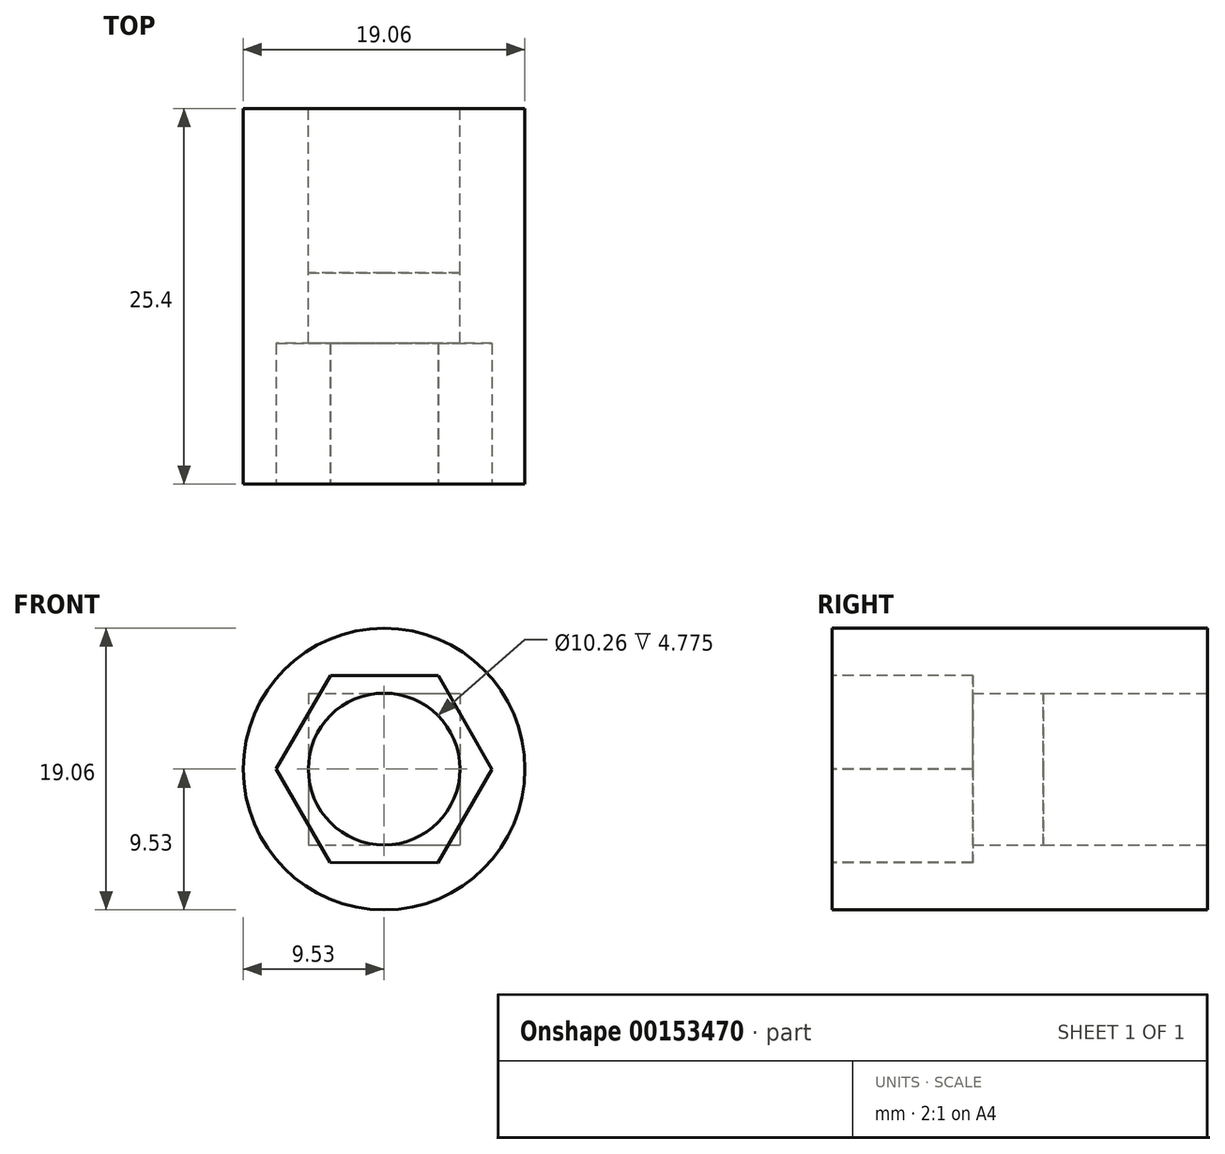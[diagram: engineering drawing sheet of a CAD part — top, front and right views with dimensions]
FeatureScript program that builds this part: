
annotation { "Feature Type Name" : "Feature", "Feature Type Description" : "" }
export const myFeature = defineFeature(function(context is Context, id is Id, definition is map)
    precondition{}
    {
        {
            var Q0;
            Q0=qCreatedBy(makeId("Front.planeOp"),FACE);
            var sketch = newSketch(context, id + "F0", { "sketchPlane" : qUnion([Q0])});
            skCircle(sketch, "E0", {"center": v(0, 0) * mm, "radius": 9.53 * mm});
            skSolve(sketch);
        }
        {
            var Q0;
            Q0 = qSketchRegion(id + "F0", true);
            extrude(context, id + "F1", {"entities" : qUnion([Q0]), "depth" : 25.4 * mm});
        }
        {
            var Q0;
            Q0=qCreatedBy(makeId("Front.planeOp"),FACE);
            var sketch = newSketch(context, id + "F2", { "sketchPlane" : qUnion([Q0])});
            skLineSegment(sketch, "E1.bottom", {"start": v(-5.13, 5.13) * mm, "end": v(5.13, 5.13) * mm});
            skLineSegment(sketch, "E1.top", {"start": v(-5.13, -5.13) * mm, "end": v(5.13, -5.13) * mm});
            skLineSegment(sketch, "E1.left", {"start": v(-5.13, 5.13) * mm, "end": v(-5.13, -5.13) * mm});
            skLineSegment(sketch, "E1.right", {"start": v(5.13, 5.13) * mm, "end": v(5.13, -5.13) * mm});
            skCircle(sketch, "E2", {"center": v(0, 0) * mm, "radius": 5.13 * mm});
            skSolve(sketch);
        }
        {
            var Q0;
            {var subQ0=sQuery(id+"F2.wireOp",EDGE,"E2");var subQ1=makeQuery(id+"F2.imprint","INTERSECT",VERTEX,{"derivedFrom":[sQuery(id+"F2.wireOp",EDGE,"E1.bottom"),subQ0]});Q0=makeQuery(id+"F2.imprint","IMPRINT",FACE,{"disambiguationData":[TD([[makeQuery(id+"F2.imprint","IMPRINT",EDGE,{"disambiguationData":[TD([[subQ1,1.0]])],"derivedFrom":subQ0}),1.0]])]});}
            extrude(context, id + "F3", {"entities" : qUnion([Q0]), "operationType" : NewBodyOperationType.REMOVE, "endBound" : BoundingType.THROUGH_ALL, "depth" : 25.4 * mm});
        }
        {
            var Q0;
            Q0 = qSketchRegion(id + "F2", true);
            extrude(context, id + "F4", {"entities" : qUnion([Q0]), "operationType" : NewBodyOperationType.REMOVE, "depth" : 11.1 * mm});
        }
        {
            var Q0;
            Q0=makeQuery(id+"F1.opExtrude","CAP_FACE",FACE,{"disambiguationData":[OSD([sQuery(id+"F0.wireOp",EDGE,"E0")])],"isStart":false});
            var sketch = newSketch(context, id + "F5", { "sketchPlane" : qUnion([Q0])});
            skSolve(sketch);
        }
        {
            var Q0;
            {var subQ0=sQuery(id+"F0.wireOp",EDGE,"E0");Q0=makeQuery(id+"F5.imprint","IMPRINT",FACE,{"disambiguationData":[TD([[makeQuery(id+"F5.imprint","IMPRINT",EDGE,{"derivedFrom":makeQuery(id+"F1.opExtrude","CAP_EDGE",EDGE,{"disambiguationData":[OSD([subQ0])],"isStart":false})}),1.0]])]});}
            var sketch = newSketch(context, id + "F6", { "sketchPlane" : qUnion([Q0])});
            skCircle(sketch, "E3.cCircle", {"center": v(0, 0) * mm, "radius": 6.32 * mm, "construction": true});
            skLineSegment(sketch, "E3.0", {"start": v(-3.66, -6.32) * mm, "end": v(-7.3, 0.01) * mm});
            skLineSegment(sketch, "E3.1", {"start": v(-7.3, 0.01) * mm, "end": v(-3.64, 6.33) * mm});
            skLineSegment(sketch, "E3.2", {"start": v(-3.64, 6.33) * mm, "end": v(3.66, 6.32) * mm});
            skLineSegment(sketch, "E3.3", {"start": v(3.66, 6.32) * mm, "end": v(7.3, -0.01) * mm});
            skLineSegment(sketch, "E3.4", {"start": v(7.3, -0.01) * mm, "end": v(3.64, -6.33) * mm});
            skLineSegment(sketch, "E3.5", {"start": v(3.64, -6.33) * mm, "end": v(-3.66, -6.32) * mm});
            skPoint(sketch, "E3.0.midPoint", {"position": v(-5.48, -3.15) * mm});
            skSolve(sketch);
        }
        {
            var Q0;
            Q0 = qSketchRegion(id + "F6", true);
            extrude(context, id + "F7", {"entities" : qUnion([Q0]), "operationType" : NewBodyOperationType.REMOVE, "oppositeDirection" : true, "depth" : 9.52 * mm});
        }
    });
